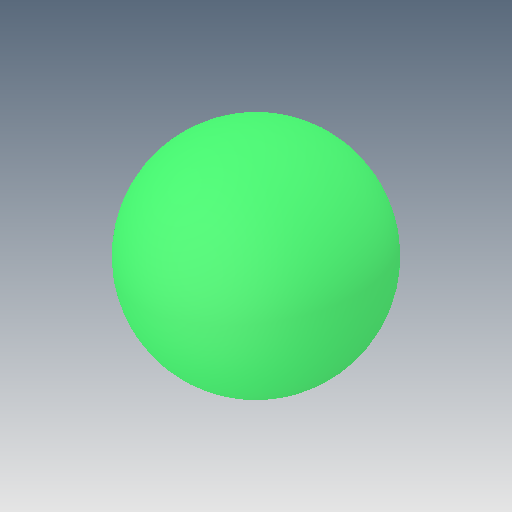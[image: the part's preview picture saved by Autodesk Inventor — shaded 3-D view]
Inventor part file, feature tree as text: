
AUTODESK INVENTOR PART (.ipt)
format: ipt  version: 2023.5 (Build 275446000, 446)  size: 125,952 bytes
history: native  units: in
note: dims shown in document units (in); Inventor stores cm internally (conversion verified against a paired STEP export)
features: revolve x1
ambient origin geometry x8: Origin, YZ Plane, XZ Plane, XY Plane, X Axis, Y Axis, Z Axis, Center Point
bodies: Solid1 (feature_tree)
feature tree (1):
  revolve  "Revolve2"  [1 undecoded]
note: 1 required parameter value undecoded (feature->parameter linkage not recoverable at this tier; creation-order binding heuristic only, values carry confidence <= 0.55)
